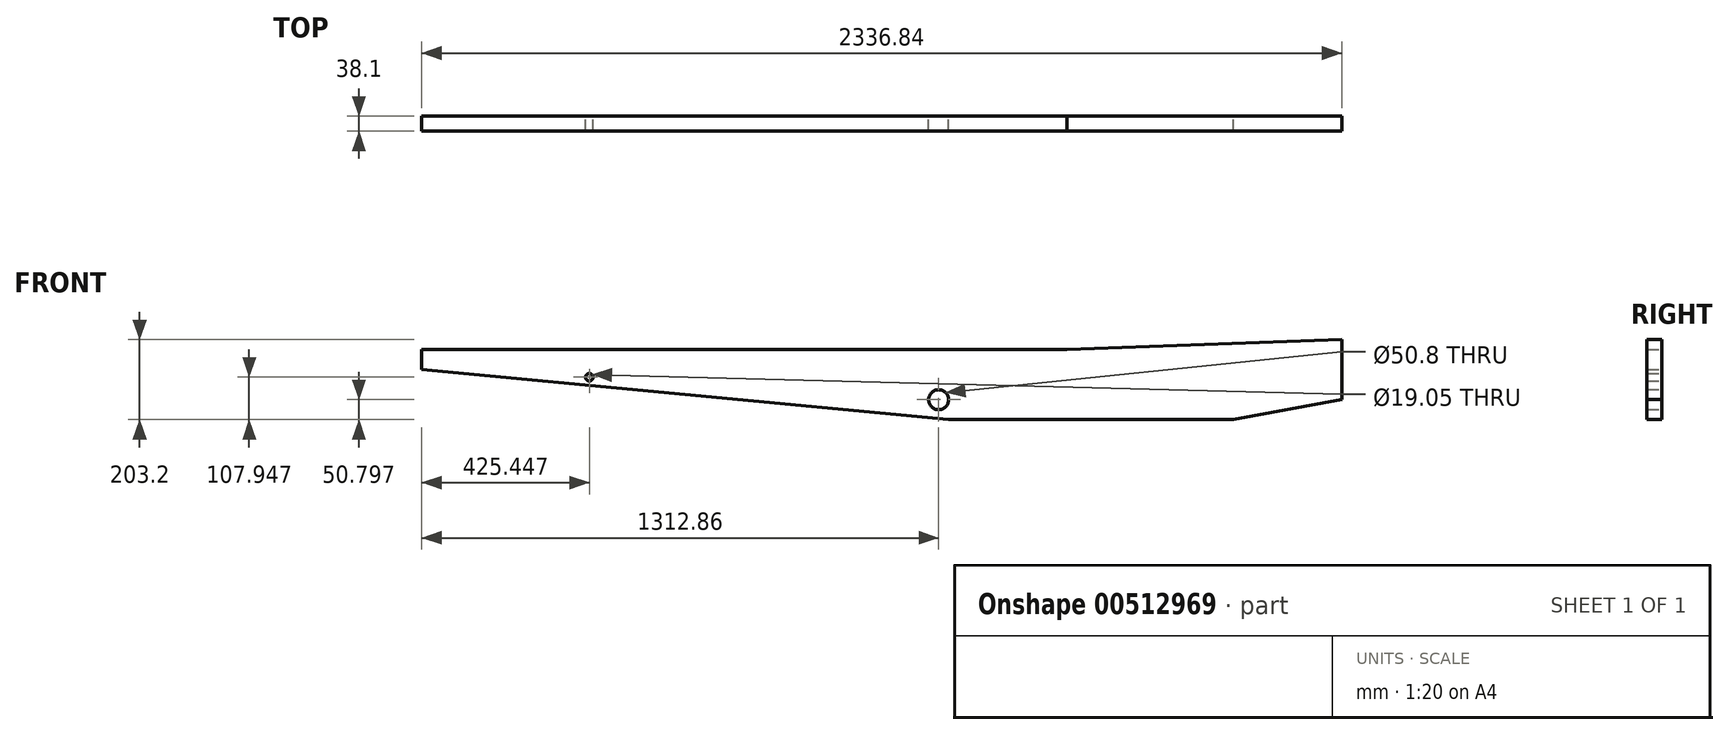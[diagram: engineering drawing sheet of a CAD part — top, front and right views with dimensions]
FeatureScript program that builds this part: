
annotation { "Feature Type Name" : "Feature", "Feature Type Description" : "" }
export const myFeature = defineFeature(function(context is Context, id is Id, definition is map)
    precondition{}
    {
        {
            var Q0;
            Q0=qCreatedBy(makeId("Front.planeOp"),FACE);
            var sketch = newSketch(context, id + "F0", { "sketchPlane" : qUnion([Q0])});
            skLineSegment(sketch, "E0", {"start": v(-1338.2, -135) * mm, "end": v(300.1, -135) * mm});
            skLineSegment(sketch, "E1", {"start": v(-1338.2, -135) * mm, "end": v(-1338.2, -185.8) * mm});
            skLineSegment(sketch, "E2", {"start": v(0, -312.8) * mm, "end": v(723.9, -312.8) * mm});
            skLineSegment(sketch, "E3", {"start": v(-1338.2, -185.8) * mm, "end": v(0, -312.8) * mm});
            skLineSegment(sketch, "E4", {"start": v(723.9, -312.8) * mm, "end": v(998.64, -262) * mm});
            skLineSegment(sketch, "E5", {"start": v(998.64, -262) * mm, "end": v(998.64, -109.6) * mm});
            skLineSegment(sketch, "E6", {"start": v(998.64, -109.6) * mm, "end": v(300.1, -135) * mm});
            skCircle(sketch, "E7", {"center": v(-25.34, -262) * mm, "radius": 25.4 * mm});
            skCircle(sketch, "E8", {"center": v(-912.75, -204.85) * mm, "radius": 9.53 * mm});
            skSolve(sketch);
        }
        {
            var Q0;
            Q0=makeQuery(id+"F0.imprint","IMPRINT",FACE,{"disambiguationData":[TD([[makeQuery(id+"F0.imprint","IMPRINT",EDGE,{"derivedFrom":sQuery(id+"F0.wireOp",EDGE,"E0")}),-1.0]])]});
            extrude(context, id + "F1", {"entities" : qUnion([Q0]), "depth" : 38.1 * mm});
        }
    });
